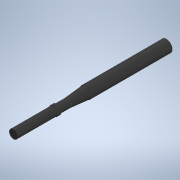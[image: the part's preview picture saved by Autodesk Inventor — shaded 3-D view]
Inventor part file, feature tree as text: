
AUTODESK INVENTOR PART (.ipt)
format: ipt  version: 2020 (Build 240168000, 168)  size: 130,560 bytes
history: native  units: mm
features: sketch x6, extrude x4, plane x1, loft x1, other x1
ambient origin geometry x8: Origin, YZ Plane, XZ Plane, XY Plane, X Axis, Y Axis, Z Axis, Center Point
bodies: Solid1 (feature_tree)
feature tree (13):
  extrude  "Extrusion1"  Depth=150.0mm TaperAngle=0.0deg
  extrude  "Extrusion2"  Depth=10.0mm TaperAngle=0.0deg
  extrude  "Extrusion3"  Depth=40.0mm TaperAngle=0.0deg
  sketch  "Sketch4"  dims[d9=70.0mm d10=30.0mm]
  plane  "Work Plane1"
  loft  "Loft1"
  extrude  "Extrusion4"  TaperAngle=0.0deg  [1 undecoded]
  sketch  "Sketch1"  dims[d0=32.0mm d1=150.0mm d2=0.0mm]
  sketch  "Sketch2"  dims[d3=35.0mm d4=10.0mm d5=0.0mm]
  sketch  "Sketch3"  dims[d6=30.0mm d7=40.0mm d8=0.0mm]
  sketch  "Sketch5"  dims[d11=42.0mm d12=0.0mm d13=90.0deg]
  other  "Edges1"
  sketch  "Sketch6"  dims[d14=0.0mm d15=90.0deg d16=44.0mm d17=300.0mm d18=0.0mm]
note: 1 required parameter value undecoded (feature->parameter linkage not recoverable at this tier; creation-order binding heuristic only, values carry confidence <= 0.55)
